# Revit family: БГЗ4_RV17_LOD400 (05.11.23)
name_source: partatom
category: Электрооборудование
revit_build: Autodesk Revit 2017 (Build: 20170118_1100(x64)
units: mm (PartAtom-declared; Revit-internal decimal feet)

## family parameters
Всегда вертикально = Нет
Конфигурация панели = Два столбца, слева направо
На основе рабочей плоскости = Да
Общий = Нет
При загрузке вырезать с полостями = Нет
Размер круглого соединителя = Использовать диаметр
Тип детали = Щит
Точка расчета площади = Нет

## types (1)
- БГЗ4
    ADSK_URL страницы изделия = https://stilsoft.ru
    ADSK_Единица измерения = шт.
    ADSK_Завод-изготовитель = ООО «Основа Безопасности»
    ADSK_Количество = 1
    ADSK_Марка = СТВФ.426471.106
    ADSK_Масса = 0.3
    ADSK_Наименование = Блок грозозащиты БГЗ4
    ADSK_Размер_Высота = 42 мм
    ADSK_Размер_Глубина = 84 мм
    ADSK_Размер_Длина = 148 мм
    d_короба = 20 мм
    Диапазон рабочих температур, °С = от –40 до +50
    Количество защищаемых линий = 4
    Максимально допустимое напряжение электропитания РоЕ, В = 57
    Напряжение = 57
    Отметка по умолчанию = 1219 мм
    Поддержка PoE = 802.3af Active / Passive
    Разъемы вход/выход = RJ45/RJ45
    Расстояние передачи данных (информации), дальность действия по кабелю UTP-5e, до, м = 100 мм
    Скорость передачи данных (информации) по кабелю UTP-5e, Мбит/с = 10/100/1000
